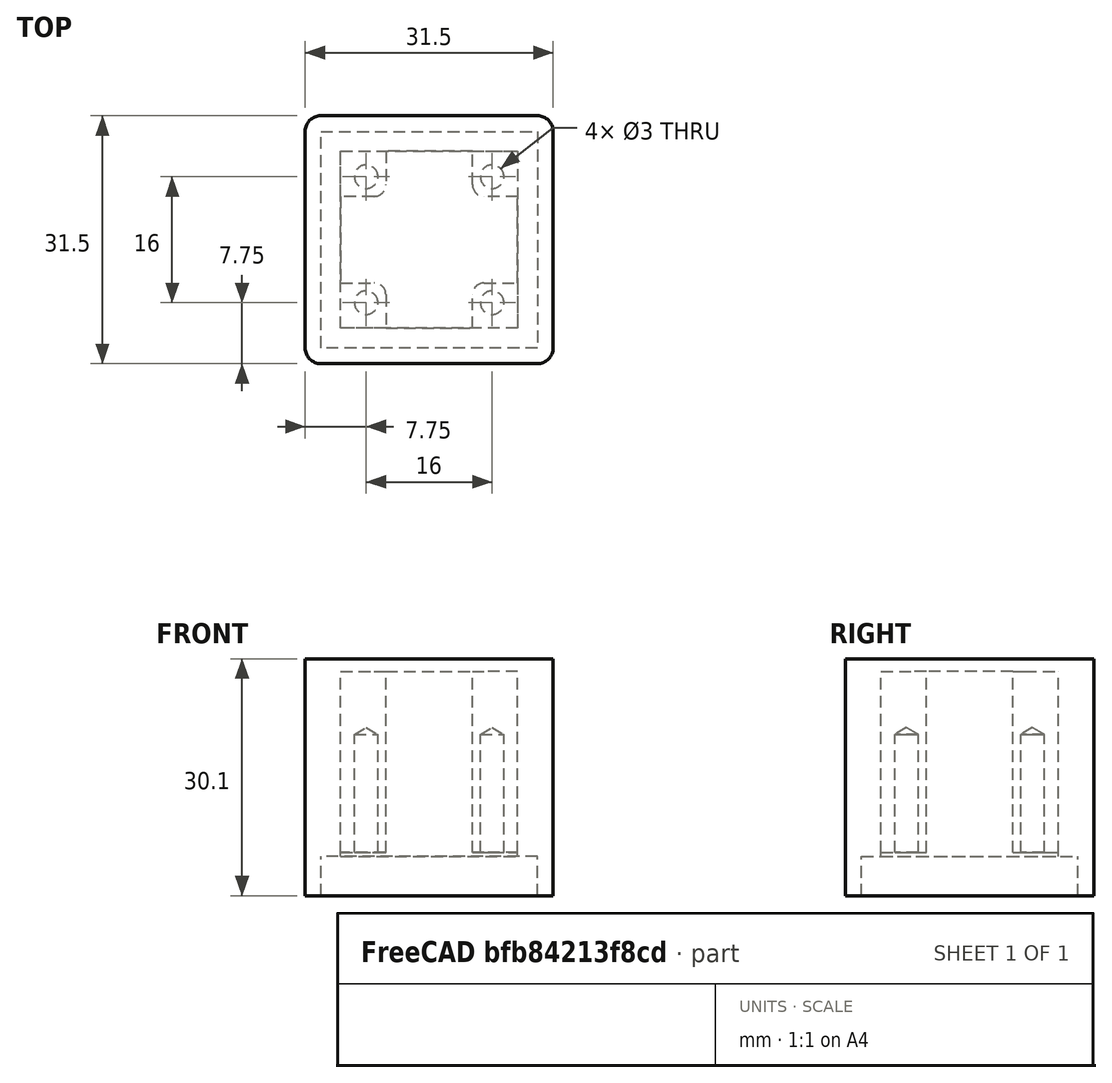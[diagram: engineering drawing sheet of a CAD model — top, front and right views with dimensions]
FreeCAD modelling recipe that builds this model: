
FCSTD DOCUMENT  (FreeCAD 1.1R44874 (Git))
Label: hood1_10x10x20
objects: Sketcher::SketchObject×5, PartDesign::Pocket×3, App::Point×1, PartDesign::Pad×1, PartDesign::Hole×1, PartDesign::Body×1, Mesh::Feature×1
note: 26 computed .brp shape members not serialized (recipe doc carries the construction recipe); baked Part::Feature solids carry a one-line shape summary decoded from their .brp

FEATURE [App::Point] Origin001
  Role = Origin
FEATURE [Sketcher::SketchObject] Sketch
  ArcFitTolerance = 1e-06
  AttachmentSupport = -> [Origin]
  ExternalTypes = [0]
  FullyConstrained = true
  MakeInternals = false
  MapMode = 5
  _ExternalGeoVersion = 1
  sketch-geometry (13):
    g0: LineSegment StartX=-13.75 StartY=-15.75 StartZ=0 EndX=13.75 EndY=-15.75 EndZ=0
    g1: LineSegment StartX=15.75 StartY=-13.75 StartZ=0 EndX=15.75 EndY=13.75 EndZ=0
    g2: LineSegment StartX=13.75 StartY=15.75 StartZ=0 EndX=-13.75 EndY=15.75 EndZ=0
    g3: LineSegment StartX=-15.75 StartY=13.75 StartZ=0 EndX=-15.75 EndY=-13.75 EndZ=0
    g4: GeomPoint [constr] X=0 Y=0 Z=0
    g5: ArcOfCircle CenterX=-13.75 CenterY=13.75 CenterZ=0 NormalX=0 NormalY=0 NormalZ=1 AngleXU=0 Radius=2 StartAngle=1.5708 EndAngle=3.14159
    g6: GeomPoint [constr] X=-15.75 Y=15.75 Z=0
    g7: ArcOfCircle CenterX=13.75 CenterY=13.75 CenterZ=0 NormalX=0 NormalY=0 NormalZ=1 AngleXU=0 Radius=2 StartAngle=0 EndAngle=1.5708
    g8: GeomPoint [constr] X=15.75 Y=15.75 Z=0
    g9: ArcOfCircle CenterX=13.75 CenterY=-13.75 CenterZ=0 NormalX=0 NormalY=0 NormalZ=1 AngleXU=0 Radius=2 StartAngle=4.71239 EndAngle=6.28319
    g10: GeomPoint [constr] X=15.75 Y=-15.75 Z=0
    g11: ArcOfCircle CenterX=-13.75 CenterY=-13.75 CenterZ=0 NormalX=0 NormalY=0 NormalZ=1 AngleXU=0 Radius=2 StartAngle=3.14159 EndAngle=4.71239
    g12: GeomPoint [constr] X=-15.75 Y=-15.75 Z=0
  constraints (28):
    c: Horizontal(g0)
    c: Horizontal(g2)
    c: Vertical(g1)
    c: Vertical(g3)
    c: Symmetric(g8,g12,g4)
    c: Distance(g10,g12) = 31.5
    c: Distance(g12,g6) = 31.5
    c: Coincident(g4,g-1)
    c: PointOnObject(g6,g3)
    c: PointOnObject(g6,g2)
    c: Tangent(g3,g5) = -1.5708
    c: Tangent(g2,g5) = -1.5708
    c: Radius(g5) = 2
    c: PointOnObject(g8,g1)
    c: PointOnObject(g8,g2)
    c: Tangent(g1,g7) = -1.5708
    c: Tangent(g2,g7) = -1.5708
    c: PointOnObject(g10,g1)
    c: PointOnObject(g10,g0)
    c: Tangent(g1,g9) = -1.5708
    c: Tangent(g0,g9) = -1.5708
    c: PointOnObject(g12,g0)
    c: PointOnObject(g12,g3)
    c: Tangent(g0,g11) = -1.5708
    c: Tangent(g3,g11) = -1.5708
    c: Equal(g5,g7)
    c: Equal(g5,g11)
    c: Equal(g5,g9)
FEATURE [PartDesign::Pad] Pad
  Direction = (0,0,1)
  Length = 30.1
  Length2 = 10
  Profile = -> Sketch
  ReferenceAxis = -> Sketch [N_Axis]
  Refine = true
  SideType = 0
  Suppressed = false
  Type = 0
  Type2 = 0
FEATURE [Sketcher::SketchObject] Sketch001
  ArcFitTolerance = 1e-06
  AttachmentSupport = -> [Pad]
  ExternalTypes = [0]
  FullyConstrained = true
  MakeInternals = false
  MapMode = 5
  Placement = pos=(0,0,0) rot=(1,0,0;3.14159rad)
  _ExternalGeoVersion = 1
  sketch-geometry (5):
    g0: LineSegment StartX=-13.75 StartY=-13.75 StartZ=0 EndX=13.75 EndY=-13.75 EndZ=0
    g1: LineSegment StartX=13.75 StartY=-13.75 StartZ=0 EndX=13.75 EndY=13.75 EndZ=0
    g2: LineSegment StartX=13.75 StartY=13.75 StartZ=0 EndX=-13.75 EndY=13.75 EndZ=0
    g3: LineSegment StartX=-13.75 StartY=13.75 StartZ=0 EndX=-13.75 EndY=-13.75 EndZ=0
    g4: GeomPoint [constr] X=0 Y=0 Z=0
  constraints (12):
    c: Coincident(g0,g1)
    c: Coincident(g1,g2)
    c: Coincident(g2,g3)
    c: Coincident(g3,g0)
    c: Horizontal(g0)
    c: Horizontal(g2)
    c: Vertical(g1)
    c: Vertical(g3)
    c: Symmetric(g2,g0,g4)
    c: Distance(g1,g3) = 27.5
    c: Distance(g0,g2) = 27.5
    c: Coincident(g4,g-1)
FEATURE [PartDesign::Pocket] Pocket
  BaseFeature = -> Pad
  Direction = (0,0,1)
  Length = 5
  Length2 = 5
  Profile = -> Sketch001
  ReferenceAxis = -> Sketch001 [N_Axis]
  Refine = true
  SideType = 0
  Suppressed = false
  Type = 0
  Type2 = 0
FEATURE [Sketcher::SketchObject] Sketch002
  ArcFitTolerance = 1e-06
  AttachmentSupport = -> [Pocket]
  ExternalTypes = [0]
  FullyConstrained = true
  MakeInternals = false
  MapMode = 5
  Placement = pos=(0,0,5) rot=(1,0,0;3.14159rad)
  _ExternalGeoVersion = 1
  sketch-geometry (5):
    g0: LineSegment StartX=-11.25 StartY=-11.25 StartZ=0 EndX=11.25 EndY=-11.25 EndZ=0
    g1: LineSegment StartX=11.25 StartY=-11.25 StartZ=0 EndX=11.25 EndY=11.25 EndZ=0
    g2: LineSegment StartX=11.25 StartY=11.25 StartZ=0 EndX=-11.25 EndY=11.25 EndZ=0
    g3: LineSegment StartX=-11.25 StartY=11.25 StartZ=0 EndX=-11.25 EndY=-11.25 EndZ=0
    g4: GeomPoint [constr] X=0 Y=0 Z=0
  constraints (12):
    c: Coincident(g0,g1)
    c: Coincident(g1,g2)
    c: Coincident(g2,g3)
    c: Coincident(g3,g0)
    c: Horizontal(g0)
    c: Horizontal(g2)
    c: Vertical(g1)
    c: Vertical(g3)
    c: Symmetric(g2,g0,g4)
    c: Distance(g1,g3) = 22.5
    c: Distance(g0,g2) = 22.5
    c: Coincident(g4,g-1)
FEATURE [PartDesign::Pocket] Pocket001
  BaseFeature = -> Pocket
  Direction = (0,0,1)
  Length = 0.5
  Length2 = 5
  Profile = -> Sketch002
  ReferenceAxis = -> Sketch002 [N_Axis]
  Refine = true
  SideType = 0
  Suppressed = false
  Type = 0
  Type2 = 0
FEATURE [Sketcher::SketchObject] Sketch003
  ArcFitTolerance = 1e-06
  AttachmentSupport = -> [Pocket001]
  ExternalTypes = [0]
  FullyConstrained = true
  MakeInternals = false
  MapMode = 5
  Placement = pos=(0,0,5.5) rot=(1,0,0;3.14159rad)
  _ExternalGeoVersion = 1
  sketch-geometry (4):
    g0: Circle CenterX=8 CenterY=8 CenterZ=0 NormalX=0 NormalY=0 NormalZ=1 AngleXU=0 Radius=1.5
    g1: Circle CenterX=-8 CenterY=8 CenterZ=0 NormalX=0 NormalY=0 NormalZ=1 AngleXU=0 Radius=1.5
    g2: Circle CenterX=-8 CenterY=-8 CenterZ=0 NormalX=0 NormalY=0 NormalZ=1 AngleXU=0 Radius=1.5
    g3: Circle CenterX=8 CenterY=-8 CenterZ=0 NormalX=0 NormalY=0 NormalZ=1 AngleXU=0 Radius=1.5
  constraints (9):
    c: Diameter(g0) = 3
    c: DistanceY(g-1,g0) = 8
    c: DistanceX(g-1,g0) = 8
    c: Equal(g0,g1)
    c: Equal(g0,g2)
    c: Equal(g0,g3)
    c: Symmetric(g1,g3,g-1)
    c: Symmetric(g0,g3,g-1)
    c: Symmetric(g2,g3,g-2)
FEATURE [PartDesign::Hole] Hole
  BaseFeature = -> Pocket001
  BaseProfileType = 7
  CustomThreadClearance = 0
  Depth = 15
  DepthType = 0
  Diameter = 3
  DrillForDepth = false
  DrillPoint = 1
  DrillPointAngle = 118
  HoleCutCountersinkAngle = 90
  HoleCutCustomValues = false
  HoleCutDepth = 0
  HoleCutDiameter = 0
  HoleCutType = 0
  ModelThread = false
  Profile = -> Sketch003
  Refine = true
  Suppressed = false
  Tapered = false
  TaperedAngle = 90
  ThreadClass = 0
  ThreadDepth = 15
  ThreadDepthType = 0
  ThreadDiameter = 3
  ThreadDirection = 0
  ThreadFit = 0
  ThreadSize = 0
  ThreadType = 0
  Threaded = false
  UseCustomThreadClearance = false
FEATURE [Sketcher::SketchObject] Sketch004
  ArcFitTolerance = 1e-06
  AttachmentSupport = -> [Hole]
  ExternalGeometry = -> [Sketch002]
  ExternalTypes = [0,0,0,0]
  FullyConstrained = true
  MakeInternals = false
  MapMode = 5
  Placement = pos=(0,0,5.5) rot=(1,0,0;3.14159rad)
  _ExternalGeoVersion = 1
  sketch-geometry (21):
    g0: GeomPoint [constr] X=0 Y=0 Z=0
    g1: LineSegment StartX=-11.25 StartY=-5.5 StartZ=0 EndX=-11.25 EndY=5.5 EndZ=0
    g2: LineSegment StartX=-11.25 StartY=5.5 StartZ=0 EndX=-7 EndY=5.5 EndZ=0
    g3: LineSegment StartX=-5.5 StartY=7 StartZ=0 EndX=-5.5 EndY=11.25 EndZ=0
    g4: LineSegment StartX=-5.5 StartY=11.25 StartZ=0 EndX=5.5 EndY=11.25 EndZ=0
    g5: LineSegment StartX=5.5 StartY=11.25 StartZ=0 EndX=5.5 EndY=7 EndZ=0
    g6: LineSegment StartX=7 StartY=5.5 StartZ=0 EndX=11.25 EndY=5.5 EndZ=0
    g7: LineSegment StartX=11.25 StartY=5.5 StartZ=0 EndX=11.25 EndY=-5.5 EndZ=0
    g8: LineSegment StartX=11.25 StartY=-5.5 StartZ=0 EndX=7 EndY=-5.5 EndZ=0
    g9: LineSegment StartX=5.5 StartY=-7 StartZ=0 EndX=5.5 EndY=-11.25 EndZ=0
    g10: LineSegment StartX=5.5 StartY=-11.25 StartZ=0 EndX=-5.5 EndY=-11.25 EndZ=0
    g11: LineSegment StartX=-5.5 StartY=-11.25 StartZ=0 EndX=-5.5 EndY=-7 EndZ=0
    g12: LineSegment StartX=-7 StartY=-5.5 StartZ=0 EndX=-11.25 EndY=-5.5 EndZ=0
    g13: ArcOfCircle CenterX=-7 CenterY=7 CenterZ=0 NormalX=0 NormalY=0 NormalZ=1 AngleXU=0 Radius=1.5 StartAngle=4.71239 EndAngle=6.28319
    g14: GeomPoint [constr] X=-5.5 Y=5.5 Z=0
    g15: ArcOfCircle CenterX=7 CenterY=7 CenterZ=0 NormalX=0 NormalY=0 NormalZ=1 AngleXU=0 Radius=1.5 StartAngle=3.14159 EndAngle=4.71239
    g16: GeomPoint [constr] X=5.5 Y=5.5 Z=0
    g17: ArcOfCircle CenterX=7 CenterY=-7 CenterZ=0 NormalX=0 NormalY=0 NormalZ=1 AngleXU=0 Radius=1.5 StartAngle=1.5708 EndAngle=3.14159
    g18: GeomPoint [constr] X=5.5 Y=-5.5 Z=0
    g19: ArcOfCircle CenterX=-7 CenterY=-7 CenterZ=0 NormalX=0 NormalY=0 NormalZ=1 AngleXU=0 Radius=1.5 StartAngle=0 EndAngle=1.5708
    g20: GeomPoint [constr] X=-5.5 Y=-5.5 Z=0
  constraints (46):
    c: Coincident(g0,g-1)
    c: Coincident(g1,g2)
    c: Horizontal(g2)
    c: Vertical(g3)
    c: Coincident(g3,g4)
    c: Coincident(g4,g5)
    c: Vertical(g5)
    c: Horizontal(g6)
    c: Coincident(g6,g7)
    c: Coincident(g7,g8)
    c: Vertical(g9)
    c: Coincident(g9,g10)
    c: Coincident(g10,g11)
    c: Coincident(g12,g1)
    c: Tangent(g4,g-3)
    c: Tangent(g1,g-4)
    c: Tangent(g7,g-6)
    c: Tangent(g10,g-5)
    c: DistanceY(g-1,g16) = 5.5
    c: DistanceX(g-1,g16) = 5.5
    c: Symmetric(g16,g18,g-1)
    c: Symmetric(g16,g14,g-2)
    c: Symmetric(g18,g20,g-2)
    c: Parallel(g6,g8)
    c: Parallel(g2,g12)
    c: Parallel(g9,g11)
    c: PointOnObject(g14,g3)
    c: PointOnObject(g14,g2)
    c: Tangent(g3,g13) = -1.5708
    c: Tangent(g2,g13) = -1.5708
    c: Radius(g13) = 1.5
    c: PointOnObject(g16,g5)
    c: PointOnObject(g16,g6)
    c: Tangent(g5,g15) = -1.5708
    c: Tangent(g6,g15) = -1.5708
    c: PointOnObject(g18,g8)
    c: PointOnObject(g18,g9)
    c: Tangent(g8,g17) = -1.5708
    c: Tangent(g9,g17) = -1.5708
    c: PointOnObject(g20,g12)
    c: PointOnObject(g20,g11)
    c: Tangent(g12,g19) = -1.5708
    c: Tangent(g11,g19) = -1.5708
    c: Equal(g13,g15)
    c: Equal(g13,g19)
    c: Equal(g13,g17)
FEATURE [PartDesign::Pocket] Pocket002
  BaseFeature = -> Hole
  Direction = (0,0,1)
  Length = 23
  Length2 = 5
  Profile = -> Sketch004
  ReferenceAxis = -> Sketch004 [N_Axis]
  Refine = true
  SideType = 0
  Suppressed = false
  Type = 0
  Type2 = 0
FEATURE [PartDesign::Body] Body
  AllowCompound = true
  Group = -> [Sketch,Pad,Sketch001,Pocket,Sketch002,Pocket001,Sketch003,Hole,Sketch004,Pocket002]
  Origin = -> Origin
  Tip = -> Pocket002
FEATURE [Mesh::Feature] Mesh  label="Body (Meshed)"
